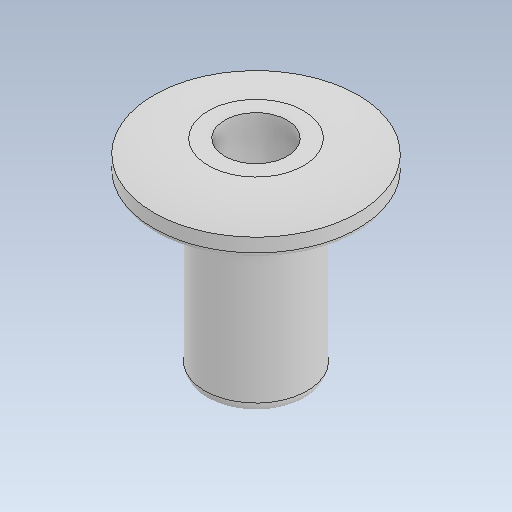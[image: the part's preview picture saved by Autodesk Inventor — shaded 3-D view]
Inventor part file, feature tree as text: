
AUTODESK INVENTOR PART (.ipt)
format: ipt  version: 2020.2 (Build 242310000, 310)  size: 119,808 bytes
history: native  units: in
note: dims shown in document units (in); Inventor stores cm internally (conversion verified against a paired STEP export)
features: fillet x1
ambient origin geometry x8: Origin, YZ Plane, XZ Plane, XY Plane, X Axis, Y Axis, Z Axis, Center Point
bodies: Solid1 (feature_tree)
feature tree (1):
  fillet  "Fillet1"  [1 undecoded]
note: 1 required parameter value undecoded (feature->parameter linkage not recoverable at this tier; creation-order binding heuristic only, values carry confidence <= 0.55)
